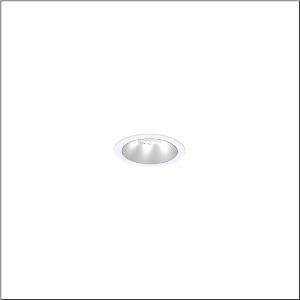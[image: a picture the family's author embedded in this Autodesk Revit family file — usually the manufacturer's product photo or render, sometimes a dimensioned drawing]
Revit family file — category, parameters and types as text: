
# Revit family: lunis_21_s_51db19ma91c
name_source: partatom
category: Lighting Fixtures
units: mm (PartAtom-declared; Revit-internal decimal feet)

## family parameters
Cut with Voids When Loaded = No
Host = Face
Light Source = No
Part Type = Normal
Room Calculation Point = No
Round Connector Dimension = Use Diameter
Shared = No

## types (1)
- --- (1 x LED, 940 lm, 5.9 W, 4000K)
    Apparent Load = 6 VA
    CIE Flux Codes = 95 100 100 100 100
    Color Rendering = 80
    Color Temperature = 4000K
    Default Elevation = 1800 mm
    Description = Lunis 21,  S, downlight, light control with lens, of PMMA, anti glare with reflector, of PC, matt, light emission: direct distribution, LED rated luminous flux: 940lm, light colour: 830/840/865, with terminal, 3-pole, mains connection: 220..240V, AC, 50..60Hz, housing, round, of diecast aluminium, traffic white (RAL 9016), diameter: 84mm, clamping range: 1..40mm, protection rating (complete): IP20, protection rating (on room side): IP54, insulation class (complete): insulation class II (safety insulation), certification: CE, impact resistance: IK03, packaging unit: 1 piece
    Height = 0 mm  [stored 0 ft]
    Lamp = 1 x LED
    Lamp Light Flux = 940 lm
    Lamp Power = 5.9 W
    Lamp count = 1
    Length = 84 mm
    Luminous efficacy = 159 lm/W
    Manufacturer = Siteco
    ModVariant = No
    Model = 51DB19MA91C
    Mounting Place = Ceiling
    Mounting Type = Recessed
    Number of Poles = 1
    OnlyDefault = Yes
    Power Factor = 1
    Product Name = Lunis 21 S
    Product group = downlight
    ProductGroupID = 400
    Protection Class = Protection class II
    Protection Degree = IP 20
    RLX_Detail_Level = 1
    RLX_Emergency_Light_Flux = 0 lm
    RLX_Emergency_Type = 0
    RLX_Emergency_Type_DB = No
    RlxData = <blob elided: 8149 chars, md5=9dd08675>
    Socket = socket
    Standby Power = 0 W
    System Light Flux = 940 lm
    System Power = 6 W
    Type Comments = factory setting: colour temperature 4000K
    Type Image = l_1290846.jpg
    URL = http://relux.com
    VarID = @adj_017533
    Voltage = 0 V
    Weight = 0.00 kg
    Width = 0 mm  [stored 0 ft]

note: [stored X ft] marks values corroborated as IEEE doubles in the binary element streams (Revit-internal decimal feet)

## geometry (parser evidence)
native form markers: Sweep x9
no freeform markers — native parametric forms only
